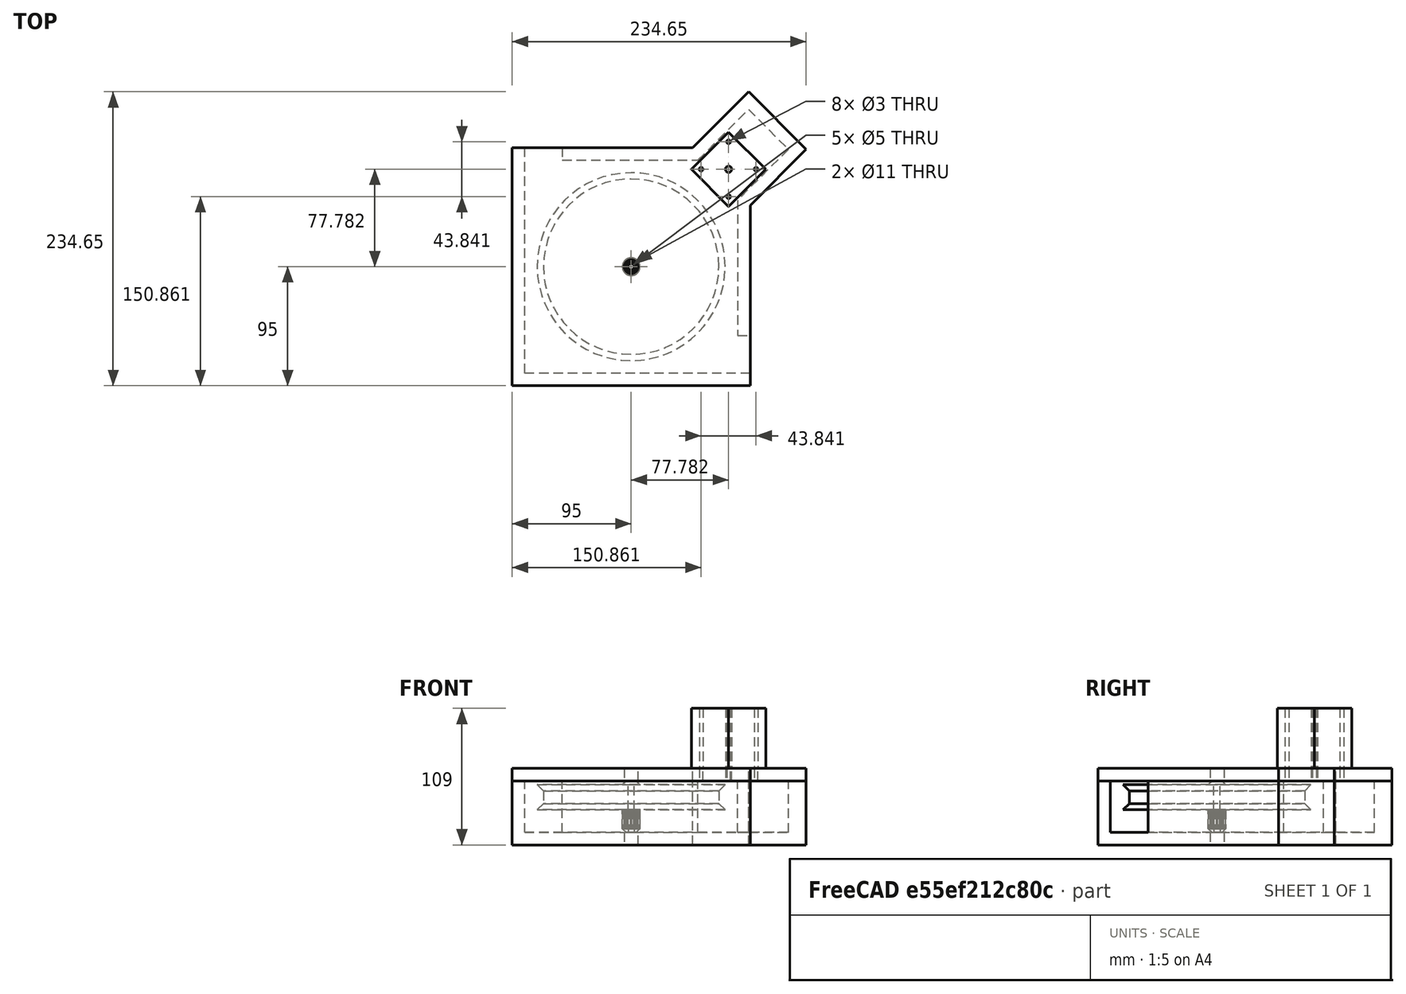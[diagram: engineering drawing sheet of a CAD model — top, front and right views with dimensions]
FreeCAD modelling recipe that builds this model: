
FCSTD DOCUMENT  (FreeCAD 1.0R39319 (Git))
Label: DogSquirrelChase
License: All rights reserved
LicenseURL: http://en.wikipedia.org/wiki/All_rights_reserved
objects: Sketcher::SketchObject×7, PartDesign::Body×5, PartDesign::Pad×4, PartDesign::Revolution×2, PartDesign::Pocket×2, Assembly::JointGroup×1, Assembly::AssemblyObject×1, Spreadsheet::Sheet×1, Part::Part2DObjectPython×1, App::Part×1
note: 44 computed .brp shape members not serialized (recipe doc carries the construction recipe); baked Part::Feature solids carry a one-line shape summary decoded from their .brp

FEATURE [Assembly::JointGroup] Joints
FEATURE [Assembly::AssemblyObject] Assembly
  Group = -> [Joints]
  Origin = -> Origin
  Type = SquirlChaseAssembly
FEATURE [Spreadsheet::Sheet] Spreadsheet
  cells = A1='DriveWheel; A2='DriveWheelDia; B2(DriveWheelDia)=150; A3='DriveWheelHeight; B3(DriveWheelHeight)=20; A4='DriveWheelLipDepth; B4(DriveWheelLipDepth)=10; A5='DriveWheelLipHeight; B5(DriveWheelLipHeight)=5; A6='DriveWheelShaftDia; B6(DriveWheelShaftDia)=5; A7='DriveWheelToWallSpace; B7(DriveWheelToWallSpace)=10; A8='DriveWheelSlotDepth; B8(DriveWheelSlotDepth)=5; A9='DriveWheelSlotLipHeight; B9(DriveWheelSlotLipHeight)=3; A10='DriveWheelBearingShoulderDia; B10(DriveWheelBearingShoulderDia)=8; A11='DriveWheelBearingShoulderHeight; B11(DriveWheelBearingShoulderHeight)=3; A12='DriveWheelSlotAngle; B12(DriveWheelSlotAngle)=45; A13='Pulleys; A14='DriveWheelPulleyDia; B14(DriveWheelPulleyDia)=44; A15='DriveWheelPulleyHeight; B15(DriveWheelPulleyHeight)=15; A16='DriveWheelPulleyTeeth; B16(DriveWheelPulleyTeeth)=20; A17='DriveWheelPulleyToothPitch; B17(DriveWheelPulleyToothPitch)=2; A18='PulleySeparationDist; B18(PulleySeparationDist)=110; A19='StepperPulleyDia; B19(StepperPulleyDia)=45; A20='StepperPulleyHeight; B20(StepperPulleyHeight)=14.5; A21='StepperPulleyTeeth; B21(StepperPulleyTeeth)=60; A23='Bearings & Holes; A24='MainDriveWheelBearingOuterDia; B24(MainDriveWheelBearingOuterDia)=11; A25='StepperMountScrewHoleDia; B25(StepperMountScrewHoleDia)=3; A26='StepperMountScrewHoleSpacing; B26(StepperMountScrewHoleSpacing)=31; A27='Enclosure; A28='MainDriveWheelMountThickness; B28(MainDriveWheelMountThickness)=10; A29='ElectronicsCompartmentDepth; B29(ElectronicsCompartmentDepth)=55; A30='EnclosureWallThickness; B30(EnclosureWallThickness)=10; A31='StringOpeningWidth; B31(StringOpeningWidth)=30; A33='Motor; A34='Nema17MotorWidth; B34(Nema17MotorWidth)=42; A35='Nema17MotorHeight; B35(Nema17MotorHeight)=48; A36='Nema17MotorShaftLength; B36(Nema17MotorShaftLength)=22; A40='TODO; A41='Calculate distance between pulley centers and add dimension; A42='Calculate thickness of bearings and assure that bottom bearing is not exposed; A43='Add Slots to allow String entry/exit
FEATURE [Sketcher::SketchObject] Sketch  label="DriveWheelProfileSketch"
  ArcFitTolerance = 1e-06
  AttachmentSupport = -> [YZ_Plane001]
  FullyConstrained = true
  MakeInternals = false
  MapMode = 5
  Placement = pos=(0,0,0) rot=(0.57735,0.57735,0.57735;2.0944rad)
  expr: Constraints[10] = Spreadsheet.DriveWheelLipHeight
  expr: Constraints[11] = Spreadsheet.DriveWheelLipHeight
  expr: Constraints[12] = Spreadsheet.DriveWheelDia / 2
  expr: Constraints[13] = Spreadsheet.DriveWheelDia / 2
  expr: Constraints[14] = Spreadsheet.DriveWheelSlotAngle
  expr: Constraints[19] = Spreadsheet.DriveWheelHeight
  expr: Constraints[23] = (Spreadsheet.DriveWheelBearingShoulderDia - Spreadsheet.DriveWheelShaftDia) / 2
  expr: Constraints[6] = Spreadsheet.DriveWheelShaftDia / 2
  expr: Constraints[9] = Spreadsheet.DriveWheelHeight + Spreadsheet.DriveWheelBearingShoulderHeight
  sketch-geometry (8):
    g0: LineSegment StartX=-2.5 StartY=0 StartZ=0 EndX=-2.5 EndY=23 EndZ=0
    g1: LineSegment StartX=-75 StartY=20 StartZ=0 EndX=-70 EndY=15 EndZ=0
    g2: LineSegment StartX=-70 StartY=15 StartZ=0 EndX=-70 EndY=5 EndZ=0
    g3: LineSegment StartX=-70 StartY=5 StartZ=0 EndX=-75 EndY=0 EndZ=0
    g4: LineSegment StartX=-75 StartY=0 StartZ=0 EndX=-2.5 EndY=0 EndZ=0
    g5: LineSegment StartX=-2.5 StartY=23 StartZ=0 EndX=-4 EndY=23 EndZ=0
    g6: LineSegment StartX=-4 StartY=23 StartZ=0 EndX=-7 EndY=20 EndZ=0
    g7: LineSegment StartX=-7 StartY=20 StartZ=0 EndX=-75 EndY=20 EndZ=0
  constraints (24):
    c: PointOnObject(g0,g-1)
    c: Vertical(g0)
    c: Coincident(g0,g5)
    c: Vertical(g2)
    c: PointOnObject(g3,g-1)
    c: Coincident(g4,g0)
    c: DistanceX(g0,g-1) = 2.5
    c: Coincident(g7,g1)
    c: Coincident(g3,g4)
    c: DistanceY(g0,g0) = 23
    c: DistanceY(g1,g7) = 5
    c: DistanceY(g3,g3) = 5
    c: DistanceX(g3,g-1) = 75
    c: DistanceX(g7,g-1) = 75
    c: Angle(g4,g3) = 0.785398
    c: Coincident(g5,g6)
    c: Horizontal(g5)
    c: Coincident(g6,g7)
    c: Horizontal(g7)
    c: DistanceY(g3,g1) = 20
    c: Coincident(g2,g1)
    c: Coincident(g2,g3)
    c: Angle(g5,g6) = 0.785398
    c: DistanceX(g5,g0) = 1.5
FEATURE [PartDesign::Revolution] Revolution  label="MainDriveWheelRevolution"
  Angle = 360
  Angle2 = 60
  Axis = (0,0,1)
  Base = (0,0,0)
  Placement = pos=(0,0,0) rot=(1,1,1;2.0944rad)
  Profile = -> Sketch
  ReferenceAxis = -> Sketch [V_Axis]
  Suppressed = false
  Type = 0
FEATURE [PartDesign::Body] Body  label="DriveWheelBody"
  AllowCompound = false
  Group = -> [Sketch,Revolution]
  Origin = -> Origin001
  Placement = pos=(0,0,-23) rot=(0,0,1;0rad)
  Tip = -> Revolution
  expr: .Placement.Base.z = (Spreadsheet.DriveWheelHeight + Spreadsheet.DriveWheelBearingShoulderHeight) * -1
FEATURE [Sketcher::SketchObject] Sketch001  label="DriveWheelShaftHoleSketch"
  ArcFitTolerance = 1e-06
  AttachmentSupport = -> [XY_Plane002]
  FullyConstrained = true
  MakeInternals = false
  MapMode = 5
  expr: Constraints[1] = Spreadsheet.DriveWheelShaftDia
  sketch-geometry (1):
    g0: Circle CenterX=0 CenterY=0 CenterZ=0 NormalX=0 NormalY=0 NormalZ=1 AngleXU=0 Radius=2.5
  constraints (2):
    c: Coincident(g0,g-1)
    c: Diameter(g0) = 5
FEATURE [Part::Part2DObjectPython] InvoluteGear  # Draft 2D object (typed FeaturePython)
  AddendumCoefficient = 1
  DedendumCoefficient = 1.25
  ExternalGear = true
  HighPrecision = true
  Modules = 0.6369
  NumberOfTeeth = 20
  PressureAngle = 1
  ProfileShiftCoefficient = 0
  RootFilletCoefficient = 0.38
  expr: NumberOfTeeth = Spreadsheet.DriveWheelPulleyTeeth
FEATURE [PartDesign::Pad] Pad  label="GearPad"
  Direction = (0,0,1)
  Length = 15
  Length2 = 10
  Profile = -> InvoluteGear
  ReferenceAxis = -> InvoluteGear [N_Axis]
  Reversed = true
  Suppressed = false
  Type = 0
  expr: Length = Spreadsheet.DriveWheelPulleyHeight
FEATURE [PartDesign::Pocket] Pocket  label="DriveWheelShaftHolePocket"
  BaseFeature = -> Pad
  Direction = (0,0,-1)
  Length = 5
  Length2 = 5
  Profile = -> Sketch001
  ReferenceAxis = -> Sketch001 [N_Axis]
  Suppressed = false
  Type = 1
FEATURE [Sketcher::SketchObject] Sketch002  label="MainWheelMountPlateSketch"
  ArcFitTolerance = 1e-06
  AttachmentOffset = pos=(0,0,20) rot=(0,0,1;0rad)
  AttachmentSupport = -> [XY_Plane004]
  FullyConstrained = true
  MakeInternals = false
  MapMode = 5
  Placement = pos=(0,0,20) rot=(0,0,1;0rad)
  expr: .AttachmentOffset.Base.z = Spreadsheet.DriveWheelHeight
  expr: Constraints[12] = Spreadsheet.MainDriveWheelBearingOuterDia
  expr: Constraints[16] = Spreadsheet.StepperMountScrewHoleSpacing
  expr: Constraints[17] = Spreadsheet.StepperMountScrewHoleSpacing
  expr: Constraints[18] = Spreadsheet.StepperMountScrewHoleSpacing
  expr: Constraints[19] = Spreadsheet.StepperMountScrewHoleSpacing
  expr: Constraints[23] = Spreadsheet.StepperMountScrewHoleDia
  expr: Constraints[24] = Spreadsheet.DriveWheelShaftDia
  expr: Constraints[25] = Spreadsheet.PulleySeparationDist
  expr: Constraints[26] = Spreadsheet.DriveWheelDia / 2 + Spreadsheet.DriveWheelToWallSpace + Spreadsheet.EnclosureWallThickness
  expr: Constraints[27] = Spreadsheet.DriveWheelDia / 2 + Spreadsheet.DriveWheelToWallSpace + Spreadsheet.EnclosureWallThickness
  expr: Constraints[28] = Spreadsheet.DriveWheelDia / 2 + Spreadsheet.DriveWheelToWallSpace + Spreadsheet.EnclosureWallThickness
  expr: Constraints[29] = Spreadsheet.DriveWheelDia / 2 + Spreadsheet.DriveWheelToWallSpace + Spreadsheet.EnclosureWallThickness
  expr: Constraints[30] = Spreadsheet.StepperPulleyDia + Spreadsheet.DriveWheelToWallSpace * 2
  expr: Constraints[36] = (Spreadsheet.StepperPulleyDia + Spreadsheet.DriveWheelToWallSpace * 2) / 2
  expr: Constraints[52] = Spreadsheet.ElectronicsCompartmentDepth
  sketch-geometry (18):
    g0: LineSegment StartX=-95 StartY=-95 StartZ=0 EndX=-95 EndY=95 EndZ=0
    g1: LineSegment StartX=-95 StartY=95 StartZ=0 EndX=49.0381 EndY=95 EndZ=0
    g2: LineSegment StartX=49.0381 StartY=95 StartZ=0 EndX=93.6916 EndY=139.654 EndZ=0
    g3: LineSegment StartX=93.6916 StartY=139.654 StartZ=0 EndX=139.654 EndY=93.6916 EndZ=0
    g4: LineSegment StartX=139.654 StartY=93.6916 StartZ=0 EndX=95 EndY=49.0381 EndZ=0
    g5: LineSegment StartX=95 StartY=49.0381 StartZ=0 EndX=95 EndY=-95 EndZ=0
    g6: LineSegment StartX=95 StartY=-95 StartZ=0 EndX=-95 EndY=-95 EndZ=0
    g7: Circle CenterX=0 CenterY=0 CenterZ=0 NormalX=0 NormalY=0 NormalZ=1 AngleXU=0 Radius=5.5
    g8: Circle CenterX=77.7817 CenterY=77.7817 CenterZ=0 NormalX=0 NormalY=0 NormalZ=1 AngleXU=0 Radius=2.5
    g9: Circle CenterX=55.8614 CenterY=77.7817 CenterZ=0 NormalX=0 NormalY=0 NormalZ=1 AngleXU=0 Radius=1.5
    g10: Circle CenterX=77.7817 CenterY=99.7021 CenterZ=0 NormalX=0 NormalY=0 NormalZ=1 AngleXU=0 Radius=1.5
    g11: Circle CenterX=99.7021 CenterY=77.7817 CenterZ=0 NormalX=0 NormalY=0 NormalZ=1 AngleXU=0 Radius=1.5
    g12: Circle CenterX=77.7817 CenterY=55.8614 CenterZ=0 NormalX=0 NormalY=0 NormalZ=1 AngleXU=0 Radius=1.5
    g13: LineSegment [constr] StartX=65.7609 StartY=111.723 StartZ=0 EndX=111.723 EndY=65.7609 EndZ=0
    g14: LineSegment [constr] StartX=116.673 StartY=116.673 StartZ=0 EndX=0 EndY=0 EndZ=0
    g15: LineSegment [constr] StartX=43.8406 StartY=89.8026 StartZ=0 EndX=89.8026 EndY=43.8406 EndZ=0
    g16: LineSegment [constr] StartX=55.8614 StartY=77.7817 StartZ=0 EndX=99.7021 EndY=77.7817 EndZ=0
    g17: LineSegment [constr] StartX=77.7817 StartY=99.7021 StartZ=0 EndX=77.7817 EndY=55.8614 EndZ=0
  constraints (53):
    c: Vertical(g0)
    c: Coincident(g1,g0)
    c: Horizontal(g1)
    c: Coincident(g3,g2)
    c: Vertical(g5)
    c: Horizontal(g6)
    c: Coincident(g6,g0)
    c: Coincident(g1,g2)
    c: Coincident(g3,g4)
    c: Coincident(g4,g5)
    c: Coincident(g5,g6)
    c: Coincident(g7,g-1)
    c: Diameter(g7) = 11
    c: Angle(g2,g1) = 2.35619
    c: Angle(g5,g4) = 2.35619
    c: Perpendicular(g2,g3)
    c: Distance(g11,g12) = 31
    c: Distance(g9,g12) = 31
    c: Distance(g11,g10) = 31
    c: Distance(g10,g9) = 31
    c: Equal(g9,g10)
    c: Equal(g9,g11)
    c: Equal(g9,g12)
    c: Diameter(g9) = 3
    c: Diameter(g8) = 5
    c: Distance(g7,g8) = 110
    c: DistanceX(g0,g7) = 95
    c: DistanceY(g0,g7) = 95
    c: DistanceX(g7,g5) = 95
    c: DistanceY(g7,g0) = 95
    c: Distance(g3,g2) = 65
    c: PointOnObject(g8,g14)
    c: Parallel(g14,g2)
    c: Parallel(g13,g3)
    c: PointOnObject(g11,g13)
    c: PointOnObject(g10,g13)
    c: Distance(g3,g14) = 32.5
    c: Coincident(g14,g7)
    c: PointOnObject(g14,g3)
    c: PointOnObject(g9,g15)
    c: PointOnObject(g12,g15)
    c: Coincident(g16,g9)
    c: Coincident(g16,g11)
    c: Horizontal(g16)
    c: PointOnObject(g8,g16)
    c: Coincident(g17,g10)
    c: Coincident(g17,g12)
    c: PointOnObject(g8,g17)
    c: PointOnObject(g15,g4)
    c: PointOnObject(g13,g4)
    c: PointOnObject(g15,g2)
    c: PointOnObject(g13,g2)
    c: Distance(g8,g14) = 55
FEATURE [Sketcher::SketchObject] Sketch003  label="MainWheelMountCoverSketch"
  ArcFitTolerance = 1e-06
  AttachmentOffset = pos=(0,0,-51) rot=(0,0,1;0rad)
  AttachmentSupport = -> [XY_Plane005]
  FullyConstrained = true
  MakeInternals = false
  MapMode = 5
  Placement = pos=(0,0,-51) rot=(0,0,1;0rad)
  expr: .AttachmentOffset.Base.z = (Spreadsheet.DriveWheelPulleyHeight + Spreadsheet.DriveWheelHeight + Spreadsheet.EnclosureWallThickness + 2 * Spreadsheet.DriveWheelBearingShoulderHeight) * -1
  expr: Constraints[12] = Spreadsheet.MainDriveWheelBearingOuterDia
  expr: Constraints[16] = Spreadsheet.DriveWheelDia / 2 + Spreadsheet.DriveWheelToWallSpace + Spreadsheet.EnclosureWallThickness
  expr: Constraints[17] = Spreadsheet.DriveWheelDia / 2 + Spreadsheet.DriveWheelToWallSpace + Spreadsheet.EnclosureWallThickness
  expr: Constraints[18] = Spreadsheet.DriveWheelDia / 2 + Spreadsheet.DriveWheelToWallSpace + Spreadsheet.EnclosureWallThickness
  expr: Constraints[19] = Spreadsheet.DriveWheelDia / 2 + Spreadsheet.DriveWheelToWallSpace + Spreadsheet.EnclosureWallThickness
  expr: Constraints[20] = Spreadsheet.StepperPulleyDia + Spreadsheet.DriveWheelToWallSpace * 2
  expr: Constraints[22] = (Spreadsheet.StepperPulleyDia + Spreadsheet.DriveWheelToWallSpace * 2) / 2
  expr: Constraints[25] = Spreadsheet.PulleySeparationDist + Spreadsheet.ElectronicsCompartmentDepth
  sketch-geometry (9):
    g0: LineSegment StartX=-95 StartY=-95 StartZ=0 EndX=-95 EndY=95 EndZ=0
    g1: LineSegment StartX=-95 StartY=95 StartZ=0 EndX=49.0381 EndY=95 EndZ=0
    g2: LineSegment StartX=49.0381 StartY=95 StartZ=0 EndX=93.6916 EndY=139.654 EndZ=0
    g3: LineSegment StartX=93.6916 StartY=139.654 StartZ=0 EndX=139.654 EndY=93.6916 EndZ=0
    g4: LineSegment StartX=139.654 StartY=93.6916 StartZ=0 EndX=95 EndY=49.0381 EndZ=0
    g5: LineSegment StartX=95 StartY=49.0381 StartZ=0 EndX=95 EndY=-95 EndZ=0
    g6: LineSegment StartX=95 StartY=-95 StartZ=0 EndX=-95 EndY=-95 EndZ=0
    g7: Circle CenterX=0 CenterY=0 CenterZ=0 NormalX=0 NormalY=0 NormalZ=1 AngleXU=0 Radius=5.5
    g8: LineSegment [constr] StartX=116.673 StartY=116.673 StartZ=0 EndX=0 EndY=0 EndZ=0
  constraints (26):
    c: Vertical(g0)
    c: Coincident(g1,g0)
    c: Horizontal(g1)
    c: Coincident(g3,g2)
    c: Vertical(g5)
    c: Horizontal(g6)
    c: Coincident(g6,g0)
    c: Coincident(g1,g2)
    c: Coincident(g3,g4)
    c: Coincident(g4,g5)
    c: Coincident(g5,g6)
    c: Coincident(g7,g-1)
    c: Diameter(g7) = 11
    c: Angle(g2,g1) = 2.35619
    c: Angle(g5,g4) = 2.35619
    c: Perpendicular(g2,g3)
    c: DistanceX(g0,g7) = 95
    c: DistanceY(g0,g7) = 95
    c: DistanceX(g7,g5) = 95
    c: DistanceY(g7,g0) = 95
    c: Distance(g3,g2) = 65
    c: Parallel(g8,g2)
    c: Distance(g3,g8) = 32.5
    c: Coincident(g8,g7)
    c: PointOnObject(g8,g3)
    c: Distance(g7,g8) = 165
FEATURE [Sketcher::SketchObject] Sketch004  label="MainWheelMountCoverCavitySketch"
  ArcFitTolerance = 1e-06
  AttachmentOffset = pos=(0,0,-41) rot=(0,0,1;0rad)
  AttachmentSupport = -> [XY_Plane005]
  FullyConstrained = true
  MakeInternals = false
  MapMode = 5
  Placement = pos=(0,0,-41) rot=(0,0,1;0rad)
  expr: .AttachmentOffset.Base.z = (Spreadsheet.DriveWheelPulleyHeight + Spreadsheet.DriveWheelHeight + 2 * Spreadsheet.DriveWheelBearingShoulderHeight) * -1
  expr: Constraints[10] = Spreadsheet.DriveWheelDia / 2 + Spreadsheet.DriveWheelToWallSpace
  expr: Constraints[11] = Spreadsheet.DriveWheelDia / 2 + Spreadsheet.DriveWheelToWallSpace
  expr: Constraints[12] = Spreadsheet.DriveWheelDia / 2 + Spreadsheet.DriveWheelToWallSpace + +Spreadsheet.EnclosureWallThickness
  expr: Constraints[13] = Spreadsheet.DriveWheelDia / 2 + Spreadsheet.DriveWheelToWallSpace + +Spreadsheet.EnclosureWallThickness
  expr: Constraints[14] = Spreadsheet.StepperPulleyDia + Spreadsheet.DriveWheelToWallSpace * 2 - 2 * Spreadsheet.EnclosureWallThickness
  expr: Constraints[16] = (Spreadsheet.StepperPulleyDia + Spreadsheet.DriveWheelToWallSpace * 2 - 2 * Spreadsheet.EnclosureWallThickness) / 2
  expr: Constraints[19] = Spreadsheet.PulleySeparationDist + Spreadsheet.ElectronicsCompartmentDepth - Spreadsheet.EnclosureWallThickness
  expr: Constraints[25] = Spreadsheet.EnclosureWallThickness
  expr: Constraints[31] = Spreadsheet.EnclosureWallThickness
  expr: Constraints[36] = Spreadsheet.StringOpeningWidth
  expr: Constraints[37] = Spreadsheet.StringOpeningWidth
  expr: Constraints[8] = Spreadsheet.MainDriveWheelBearingOuterDia
  sketch-geometry (13):
    g0: LineSegment StartX=-85 StartY=-85 StartZ=0 EndX=-85 EndY=95 EndZ=0
    g1: LineSegment StartX=53.1802 StartY=85 StartZ=0 EndX=93.6916 EndY=125.511 EndZ=0
    g2: LineSegment StartX=93.6916 StartY=125.511 StartZ=0 EndX=125.511 EndY=93.6916 EndZ=0
    g3: LineSegment StartX=125.511 StartY=93.6916 StartZ=0 EndX=85 EndY=53.1802 EndZ=0
    g4: LineSegment StartX=95 StartY=-85 StartZ=0 EndX=-85 EndY=-85 EndZ=0
    g5: Circle CenterX=0 CenterY=0 CenterZ=0 NormalX=0 NormalY=0 NormalZ=1 AngleXU=0 Radius=5.5
    g6: LineSegment [constr] StartX=109.602 StartY=109.602 StartZ=0 EndX=0 EndY=0 EndZ=0
    g7: LineSegment StartX=95 StartY=-55 StartZ=0 EndX=95 EndY=-85 EndZ=0
    g8: LineSegment StartX=85 StartY=53.1802 StartZ=0 EndX=85 EndY=-55 EndZ=0
    g9: LineSegment StartX=85 StartY=-55 StartZ=0 EndX=95 EndY=-55 EndZ=0
    g10: LineSegment StartX=-85 StartY=95 StartZ=0 EndX=-55 EndY=95 EndZ=0
    g11: LineSegment StartX=-55 StartY=95 StartZ=0 EndX=-55 EndY=85 EndZ=0
    g12: LineSegment StartX=-55 StartY=85 StartZ=0 EndX=53.1802 EndY=85 EndZ=0
  constraints (38):
    c: Vertical(g0)
    c: Coincident(g2,g1)
    c: Horizontal(g4)
    c: Coincident(g4,g0)
    c: Coincident(g12,g1)
    c: Coincident(g2,g3)
    c: Coincident(g3,g8)
    c: Coincident(g5,g-1)
    c: Diameter(g5) = 11
    c: Perpendicular(g1,g2)
    c: DistanceX(g0,g5) = 85
    c: DistanceY(g0,g5) = 85
    c: DistanceX(g5,g4) = 95
    c: DistanceY(g5,g0) = 95
    c: Distance(g2,g1) = 45
    c: Parallel(g6,g1)
    c: Distance(g2,g6) = 22.5
    c: Coincident(g6,g5)
    c: PointOnObject(g6,g2)
    c: Distance(g5,g6) = 155
    c: Coincident(g9,g7)
    c: Vertical(g7)
    c: Coincident(g8,g9)
    c: Vertical(g8)
    c: Horizontal(g9)
    c: DistanceX(g8,g7) = 10
    c: Coincident(g10,g11)
    c: Horizontal(g10)
    c: Coincident(g11,g12)
    c: Horizontal(g12)
    c: Vertical(g11)
    c: DistanceY(g11,g10) = 10
    c: Angle(g1,g12) = 2.35619
    c: Angle(g8,g3) = 2.35619
    c: Coincident(g0,g10)
    c: Coincident(g4,g7)
    c: DistanceY(g4,g7) = 30
    c: DistanceX(g0,g10) = 30
FEATURE [PartDesign::Pad] Pad003  label="MainWheelMountPlatePad"
  Direction = (0,0,1)
  Length = 10
  Length2 = 10
  Profile = -> Sketch002
  ReferenceAxis = -> Sketch002 [N_Axis]
  Suppressed = false
  Type = 0
  expr: Length = Spreadsheet.MainDriveWheelMountThickness
FEATURE [PartDesign::Body] Body002  label="DriveWheelMountPlateBody"
  AllowCompound = false
  Group = -> [Sketch002,Pad003]
  Origin = -> Origin004
  Placement = pos=(0,0,-20) rot=(0,0,1;0rad)
  Tip = -> Pad003
  expr: .Placement.Base.z = Spreadsheet.DriveWheelHeight * -1
FEATURE [PartDesign::Pad] Pad004  label="MainWheelMountCoverPad"
  Direction = (0,0,1)
  Length = 51
  Length2 = 10
  Profile = -> Sketch003
  ReferenceAxis = -> Sketch003 [N_Axis]
  Suppressed = false
  Type = 0
  expr: Length = Spreadsheet.DriveWheelPulleyHeight + Spreadsheet.DriveWheelHeight + Spreadsheet.EnclosureWallThickness + 2 * Spreadsheet.DriveWheelBearingShoulderHeight
FEATURE [PartDesign::Pocket] Pocket001  label="MainWheelMountCoverCavityPocket"
  BaseFeature = -> Pad004
  Direction = (0,0,-1)
  Length = 41
  Length2 = 5
  Profile = -> Sketch004
  ReferenceAxis = -> Sketch004 [N_Axis]
  Reversed = true
  Suppressed = false
  Type = 0
  expr: Length = Spreadsheet.DriveWheelHeight + Spreadsheet.DriveWheelPulleyHeight + 2 * Spreadsheet.DriveWheelBearingShoulderHeight
FEATURE [PartDesign::Body] Body003  label="DriveWheelMountCaseBody"
  AllowCompound = false
  Group = -> [Sketch004,Sketch003,Pad004,Pocket001]
  Origin = -> Origin005
  Tip = -> Pocket001
FEATURE [Sketcher::SketchObject] Sketch005  label="PulleyShoulderSketch"
  ArcFitTolerance = 1e-06
  AttachmentSupport = -> [YZ_Plane002]
  FullyConstrained = true
  MakeInternals = false
  MapMode = 5
  Placement = pos=(0,0,0) rot=(0.57735,0.57735,0.57735;2.0944rad)
  expr: Constraints[10] = Spreadsheet.DriveWheelPulleyHeight
  expr: Constraints[11] = Spreadsheet.DriveWheelShaftDia / 2
  expr: Constraints[7] = (Spreadsheet.DriveWheelBearingShoulderDia - Spreadsheet.DriveWheelShaftDia) / 2
  expr: Constraints[8] = Spreadsheet.DriveWheelBearingShoulderHeight
  sketch-geometry (4):
    g0: LineSegment StartX=-2.5 StartY=-15 StartZ=0 EndX=-2.5 EndY=-18 EndZ=0
    g1: LineSegment StartX=-2.5 StartY=-18 StartZ=0 EndX=-4 EndY=-18 EndZ=0
    g2: LineSegment StartX=-4 StartY=-18 StartZ=0 EndX=-7 EndY=-15 EndZ=0
    g3: LineSegment StartX=-7 StartY=-15 StartZ=0 EndX=-2.5 EndY=-15 EndZ=0
  constraints (12):
    c: Coincident(g1,g0)
    c: Horizontal(g1)
    c: Coincident(g2,g1)
    c: Coincident(g3,g0)
    c: Horizontal(g3)
    c: Coincident(g2,g3)
    c: Vertical(g0)
    c: DistanceX(g1,g0) = 1.5
    c: DistanceY(g0,g0) = 3
    c: Angle(g2,g3) = 0.785398
    c: DistanceY(g0,g-1) = 15
    c: DistanceX(g0,g-1) = 2.5
FEATURE [PartDesign::Revolution] Revolution001  label="PulleyShoulderRevolution"
  Angle = 360
  Angle2 = 60
  Axis = (0,0,1)
  Base = (0,0,0)
  BaseFeature = -> Pocket
  Profile = -> Sketch005
  ReferenceAxis = -> Sketch005 [V_Axis]
  Suppressed = false
  Type = 0
FEATURE [PartDesign::Body] Body001  label="DriveWheelPulleyBody"
  AllowCompound = false
  Group = -> [Sketch001,InvoluteGear,Pad,Pocket,Sketch005,Revolution001]
  Origin = -> Origin002
  Placement = pos=(0,0,-23) rot=(0,0,1;0rad)
  Tip = -> Revolution001
  expr: .Placement.Base.z = (Spreadsheet.DriveWheelHeight + Spreadsheet.DriveWheelBearingShoulderHeight) * -1
FEATURE [Sketcher::SketchObject] Sketch006  label="NemaMotorSketch"
  ArcFitTolerance = 1e-06
  AttachmentOffset = pos=(0,0,0) rot=(0,0,1;0.785398rad)
  AttachmentSupport = -> [XY_Plane006]
  FullyConstrained = true
  MakeInternals = false
  MapMode = 5
  Placement = pos=(0,0,0) rot=(0,0,1;0.785398rad)
  expr: Constraints[12] = (Spreadsheet.Nema17MotorWidth - Spreadsheet.StepperMountScrewHoleSpacing) / 2
  expr: Constraints[13] = (Spreadsheet.Nema17MotorWidth - Spreadsheet.StepperMountScrewHoleSpacing) / 2
  expr: Constraints[14] = (Spreadsheet.Nema17MotorWidth - Spreadsheet.StepperMountScrewHoleSpacing) / 2
  expr: Constraints[15] = (Spreadsheet.Nema17MotorWidth - Spreadsheet.StepperMountScrewHoleSpacing) / 2
  expr: Constraints[16] = (Spreadsheet.Nema17MotorWidth - Spreadsheet.StepperMountScrewHoleSpacing) / 2
  expr: Constraints[17] = (Spreadsheet.Nema17MotorWidth - Spreadsheet.StepperMountScrewHoleSpacing) / 2
  expr: Constraints[18] = (Spreadsheet.Nema17MotorWidth - Spreadsheet.StepperMountScrewHoleSpacing) / 2
  expr: Constraints[19] = (Spreadsheet.Nema17MotorWidth - Spreadsheet.StepperMountScrewHoleSpacing) / 2
  expr: Constraints[20] = Spreadsheet.Nema17MotorWidth / 2
  expr: Constraints[21] = Spreadsheet.Nema17MotorWidth
  expr: Constraints[22] = Spreadsheet.Nema17MotorWidth
  expr: Constraints[24] = Spreadsheet.PulleySeparationDist
  expr: Constraints[25] = Spreadsheet.Nema17MotorWidth / 2
  expr: Constraints[26] = Spreadsheet.DriveWheelShaftDia
  expr: Constraints[4] = Spreadsheet.Nema17MotorWidth
  expr: Constraints[5] = Spreadsheet.StepperMountScrewHoleDia
  sketch-geometry (9):
    g0: LineSegment StartX=89 StartY=21 StartZ=0 EndX=89 EndY=-21 EndZ=0
    g1: LineSegment StartX=89 StartY=-21 StartZ=0 EndX=131 EndY=-21 EndZ=0
    g2: LineSegment StartX=131 StartY=-21 StartZ=0 EndX=131 EndY=21 EndZ=0
    g3: LineSegment StartX=131 StartY=21 StartZ=0 EndX=89 EndY=21 EndZ=0
    g4: Circle CenterX=94.5 CenterY=15.5 CenterZ=0 NormalX=0 NormalY=0 NormalZ=1 AngleXU=0 Radius=1.5
    g5: Circle CenterX=125.5 CenterY=15.5 CenterZ=0 NormalX=0 NormalY=0 NormalZ=1 AngleXU=0 Radius=1.5
    g6: Circle CenterX=94.5 CenterY=-15.5 CenterZ=0 NormalX=0 NormalY=0 NormalZ=1 AngleXU=0 Radius=1.5
    g7: Circle CenterX=125.5 CenterY=-15.5 CenterZ=0 NormalX=0 NormalY=0 NormalZ=1 AngleXU=0 Radius=1.5
    g8: Circle CenterX=110 CenterY=0 CenterZ=0 NormalX=0 NormalY=0 NormalZ=1 AngleXU=0 Radius=2.5
  constraints (27):
    c: Coincident(g0,g1)
    c: Coincident(g1,g2)
    c: Coincident(g2,g3)
    c: Coincident(g3,g0)
    c: DistanceX(g0,g1) = 42
    c: Diameter(g4) = 3
    c: Equal(g5,g7)
    c: Equal(g7,g6)
    c: Equal(g6,g4)
    c: Perpendicular(g0,g1)
    c: Perpendicular(g3,g2)
    c: Perpendicular(g2,g1)
    c: Distance(g5,g3) = 5.5
    c: Distance(g5,g2) = 5.5
    c: Distance(g4,g0) = 5.5
    c: Distance(g4,g3) = 5.5
    c: Distance(g7,g1) = 5.5
    c: Distance(g7,g2) = 5.5
    c: Distance(g6,g1) = 5.5
    c: Distance(g6,g0) = 5.5
    c: Distance(g8,g1) = 21
    c: Distance(g1,g0) = 42
    c: Distance(g2,g1) = 42
    c: PointOnObject(g8,g-1)
    c: Distance(g-1,g8) = 110
    c: Distance(g8,g0) = 21
    c: Diameter(g8) = 5
FEATURE [PartDesign::Pad] Pad005  label="NemaMotorPad"
  Direction = (0,0,1)
  Length = 48
  Length2 = 10
  Profile = -> Sketch006
  ReferenceAxis = -> Sketch006 [N_Axis]
  Suppressed = false
  Type = 0
  expr: Length = Spreadsheet.Nema17MotorHeight
FEATURE [PartDesign::Body] Body004  label="DriveMotorBody"
  AllowCompound = false
  Group = -> [Sketch006,Pad005]
  Origin = -> Origin006
  Placement = pos=(0,0,10) rot=(0,0,1;0rad)
  Tip = -> Pad005
  expr: .Placement.Base.z = Spreadsheet.EnclosureWallThickness
FEATURE [App::Part] Part  label="MainDriveWheelPart"
  Group = -> [Body001,Body,Body002,Body003,Body004]
  Origin = -> Origin003
